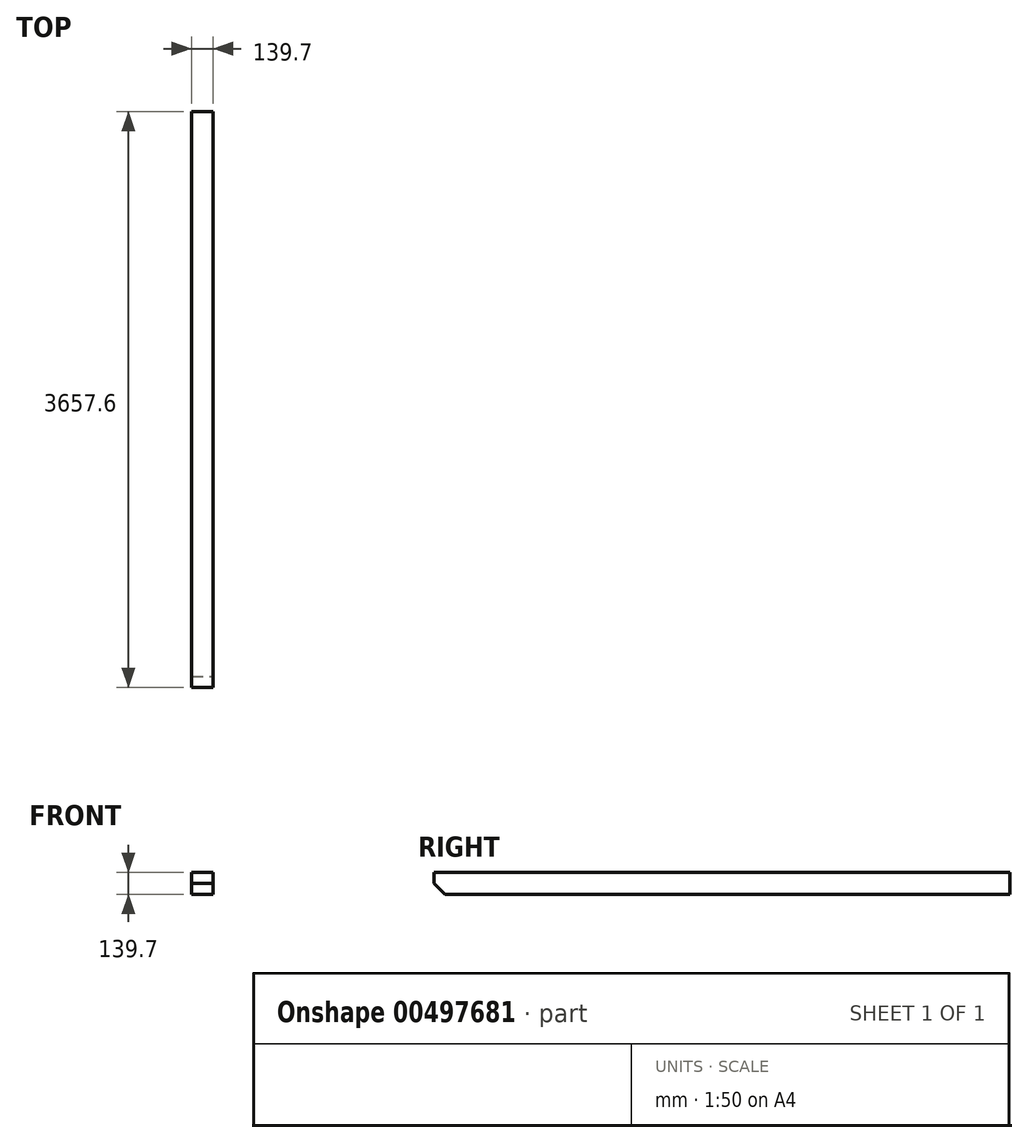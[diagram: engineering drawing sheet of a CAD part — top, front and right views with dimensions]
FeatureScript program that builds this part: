
annotation { "Feature Type Name" : "Feature", "Feature Type Description" : "" }
export const myFeature = defineFeature(function(context is Context, id is Id, definition is map)
    precondition{}
    {
        {
            var Q0;
            Q0=qCreatedBy(makeId("Front.planeOp"),FACE);
            var sketch = newSketch(context, id + "F0", { "sketchPlane" : qUnion([Q0])});
            skLineSegment(sketch, "E0.bottom", {"start": v(0, 0) * mm, "end": v(139.7, 0) * mm});
            skLineSegment(sketch, "E0.top", {"start": v(0, 139.7) * mm, "end": v(139.7, 139.7) * mm});
            skLineSegment(sketch, "E0.left", {"start": v(0, 0) * mm, "end": v(0, 139.7) * mm});
            skLineSegment(sketch, "E0.right", {"start": v(139.7, 0) * mm, "end": v(139.7, 139.7) * mm});
            skSolve(sketch);
        }
        {
            var Q0;
            Q0 = qSketchRegion(id + "F0", true);
            extrude(context, id + "F1", {"entities" : qUnion([Q0]), "depth" : 3657.6 * mm});
        }
        {
            var Q0;
            Q0=makeQuery(id+"F1.opExtrude","SWEPT_FACE",FACE,{"disambiguationData":[OSD([sQuery(id+"F0.wireOp",EDGE,"E0.right")])]});
            var sketch = newSketch(context, id + "F2", { "sketchPlane" : qUnion([Q0])});
            skLineSegment(sketch, "E1", {"start": v(-3657.6, 0) * mm, "end": v(-3657.6, 69.85) * mm});
            skLineSegment(sketch, "E2", {"start": v(-3657.6, 69.85) * mm, "end": v(-3587.75, 0) * mm});
            skLineSegment(sketch, "E3", {"start": v(-3587.75, 0) * mm, "end": v(-3657.6, 0) * mm});
            skSolve(sketch);
        }
        {
            var Q0;
            Q0 = qSketchRegion(id + "F2", true);
            extrude(context, id + "F3", {"entities" : qUnion([Q0]), "operationType" : NewBodyOperationType.REMOVE, "endBound" : BoundingType.THROUGH_ALL, "oppositeDirection" : true, "depth" : 25.4 * mm});
        }
    });
